# Revit family: Plum Fix_Waste_Argent_Pop Up Waste 32mm
name_source: partatom
category: Plumbing Fixtures
revit_build: Autodesk Revit 2016 (Build: 20150220_1215(x64)
units: mm (PartAtom-declared; Revit-internal decimal feet)

## family parameters
Always vertical = Yes
Cut with Voids When Loaded = No
OmniClass Number = 23.45.55.21
OmniClass Title = Drains (Wastes)
Part Type = Normal
Room Calculation Point = No
Round Connector Dimension = Use Diameter
Shared = No
Work Plane-Based = No

## types (1)
- Chrome
    Body Material = z_Argent_Chrome
    CW Connection = No
    CWFU = 0
    Cost = 0 $
    Description = Pop-Up Waste 32mm 2 Piece
    HW Connection = No
    HWFU = 0
    Manufacturer = Argent
    Manufacturer_Overall Depth = 65 mm
    Manufacturer_Overall Height = 65 mm
    Manufacturer_Overall Width = 65 mm
    Manufacturer_Spec Code = K316-D
    Manufacturer_URL__Product Specific = https://www.argentaust.com.au
    Model = K316-D
    ModifiedIssue_ANZRS = 20190423 $
    Type Comments = Chrome finish
    URL = https://www.argentaust.com.au
    Vent Connection = No
    WFU = 0
    Waste Connection = Yes

## geometry (parser evidence)
native form markers: Sweep x2
no freeform markers — native parametric forms only
